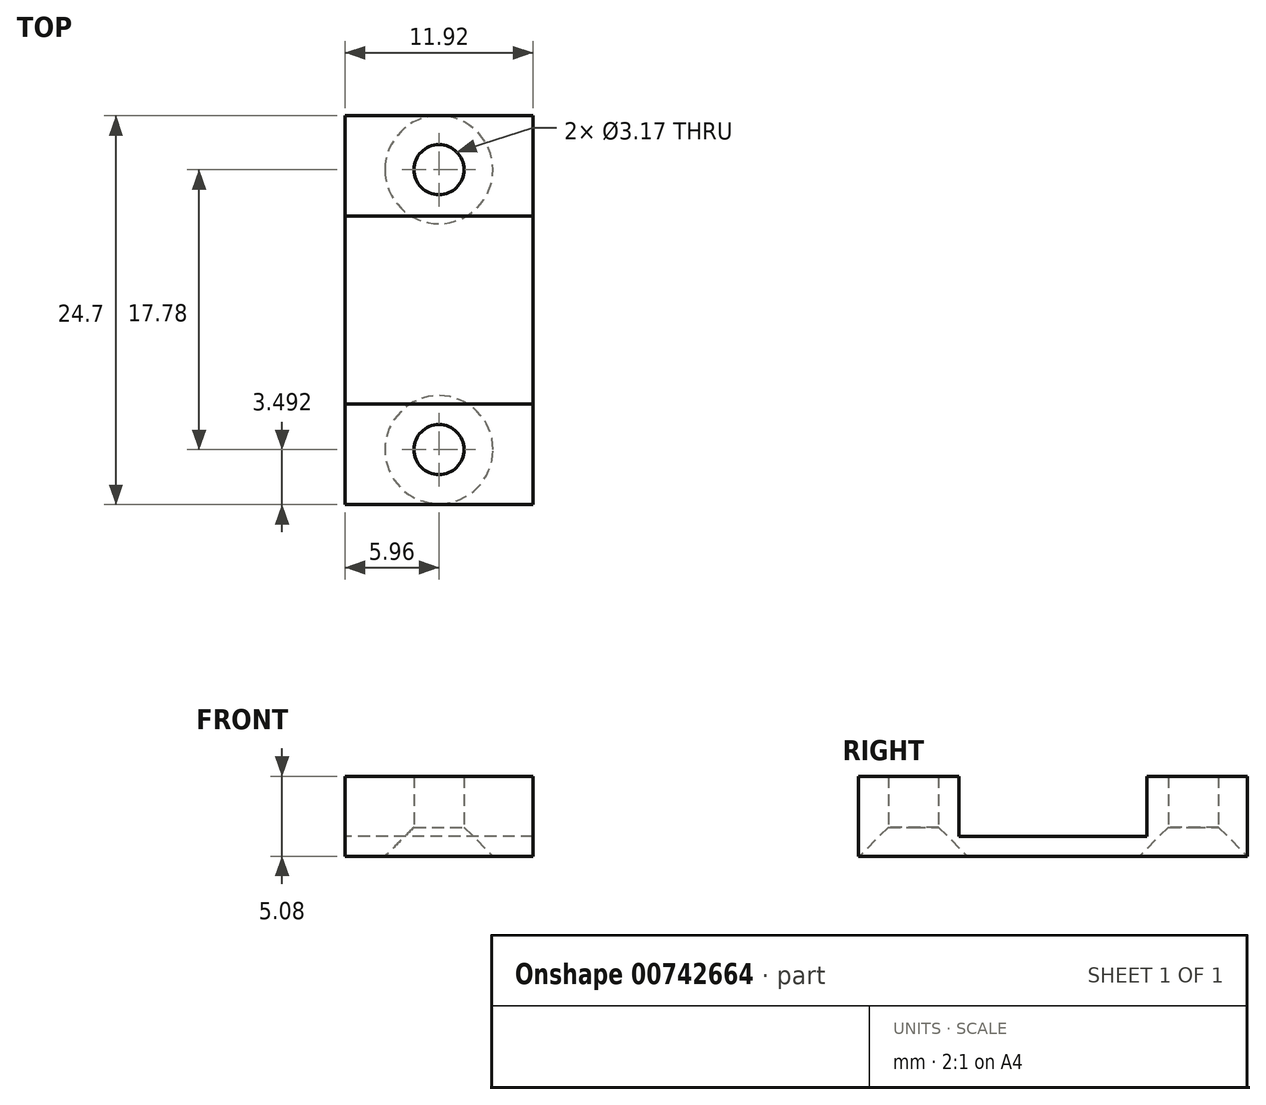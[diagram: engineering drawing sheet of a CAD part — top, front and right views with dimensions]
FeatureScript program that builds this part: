
annotation { "Feature Type Name" : "Feature", "Feature Type Description" : "" }
export const myFeature = defineFeature(function(context is Context, id is Id, definition is map)
    precondition{}
    {
        {
            var Q0;
            Q0=qCreatedBy(makeId("Top.planeOp"),FACE);
            var sketch = newSketch(context, id + "F0", { "sketchPlane" : qUnion([Q0])});
            skLineSegment(sketch, "E0.bottom", {"start": v(5.96, 12.35) * mm, "end": v(-5.96, 12.35) * mm});
            skLineSegment(sketch, "E0.top", {"start": v(5.96, -12.35) * mm, "end": v(-5.96, -12.35) * mm});
            skLineSegment(sketch, "E0.left", {"start": v(5.96, 12.35) * mm, "end": v(5.96, -12.35) * mm});
            skLineSegment(sketch, "E0.right", {"start": v(-5.96, 12.35) * mm, "end": v(-5.96, -12.35) * mm});
            skPoint(sketch, "E0.middle", {"position": v(0, 0) * mm});
            skPoint(sketch, "E1", {"position": v(0, 8.92) * mm});
            skPoint(sketch, "E2", {"position": v(0, -8.86) * mm});
            skLineSegment(sketch, "E3.bottom", {"start": v(5.96, 5.97) * mm, "end": v(-5.96, 5.97) * mm});
            skLineSegment(sketch, "E3.top", {"start": v(5.96, -5.97) * mm, "end": v(-5.96, -5.97) * mm});
            skLineSegment(sketch, "E3.left", {"start": v(5.96, 5.97) * mm, "end": v(5.96, -5.97) * mm});
            skLineSegment(sketch, "E3.right", {"start": v(-5.96, 5.97) * mm, "end": v(-5.96, -5.97) * mm});
            skSolve(sketch);
        }
        {
            var Q0;
            Q0=makeQuery(id+"F0.imprint","IMPRINT",FACE,{"disambiguationData":[TD([[makeQuery(id+"F0.imprint","IMPRINT",EDGE,{"derivedFrom":sQuery(id+"F0.wireOp",EDGE,"E3.bottom")}),1.0]])]});
            extrude(context, id + "F1", {"entities" : qUnion([Q0]), "depth" : 1.27 * mm, "offsetDistance" : 25.4 * mm});
        }
        {
            var Q0;
            {var subQ0=sQuery(id+"F0.wireOp",EDGE,"E0.top");Q0=makeQuery(id+"F0.imprint","IMPRINT",FACE,{"disambiguationData":[TD([[makeQuery(id+"F0.imprint","IMPRINT",EDGE,{"derivedFrom":subQ0}),-1.0]])]});}
            var Q1;
            {var subQ0=sQuery(id+"F0.wireOp",EDGE,"E0.bottom");Q1=makeQuery(id+"F0.imprint","IMPRINT",FACE,{"disambiguationData":[TD([[makeQuery(id+"F0.imprint","IMPRINT",EDGE,{"derivedFrom":subQ0}),1.0]])]});}
            extrude(context, id + "F2", {"entities" : qUnion([Q0, Q1]), "operationType" : NewBodyOperationType.ADD, "depth" : 5.08 * mm, "offsetDistance" : 25.4 * mm});
        }
        {
            var Q0;
            Q0=sQuery(id+"F0.wireOp",VERTEX,"E2");
            var Q1;
            Q1=sQuery(id+"F0.wireOp",VERTEX,"E1");
            var Q2;
            Q2=makeQuery(id+"F1.opExtrude","SWEPT_BODY",BODY,{"disambiguationData":[OSD([sQuery(id+"F0.wireOp",EDGE,"E0.left"),sQuery(id+"F0.wireOp",EDGE,"E0.right"),sQuery(id+"F0.wireOp",EDGE,"E3.bottom"),sQuery(id+"F0.wireOp",EDGE,"E3.top")])]});
            hole(context, id + "F3", {"style" : HoleStyle.C_SINK, "endStyle" : HoleEndStyle.THROUGH, "oppositeDirection" : true, "holeDiameter" : 3.17 * mm, "cSinkDiameter" : 6.86 * mm, "cSinkAngle" : 90 * degree, "majorDiameter" : 6.35 * mm, "isTappedThrough" : true, "tappedDepth" : 12.7 * mm, "tapClearance" : 3, "locations" : qUnion([Q0, Q1]), "scope" : qUnion([Q2])});
        }
    });
